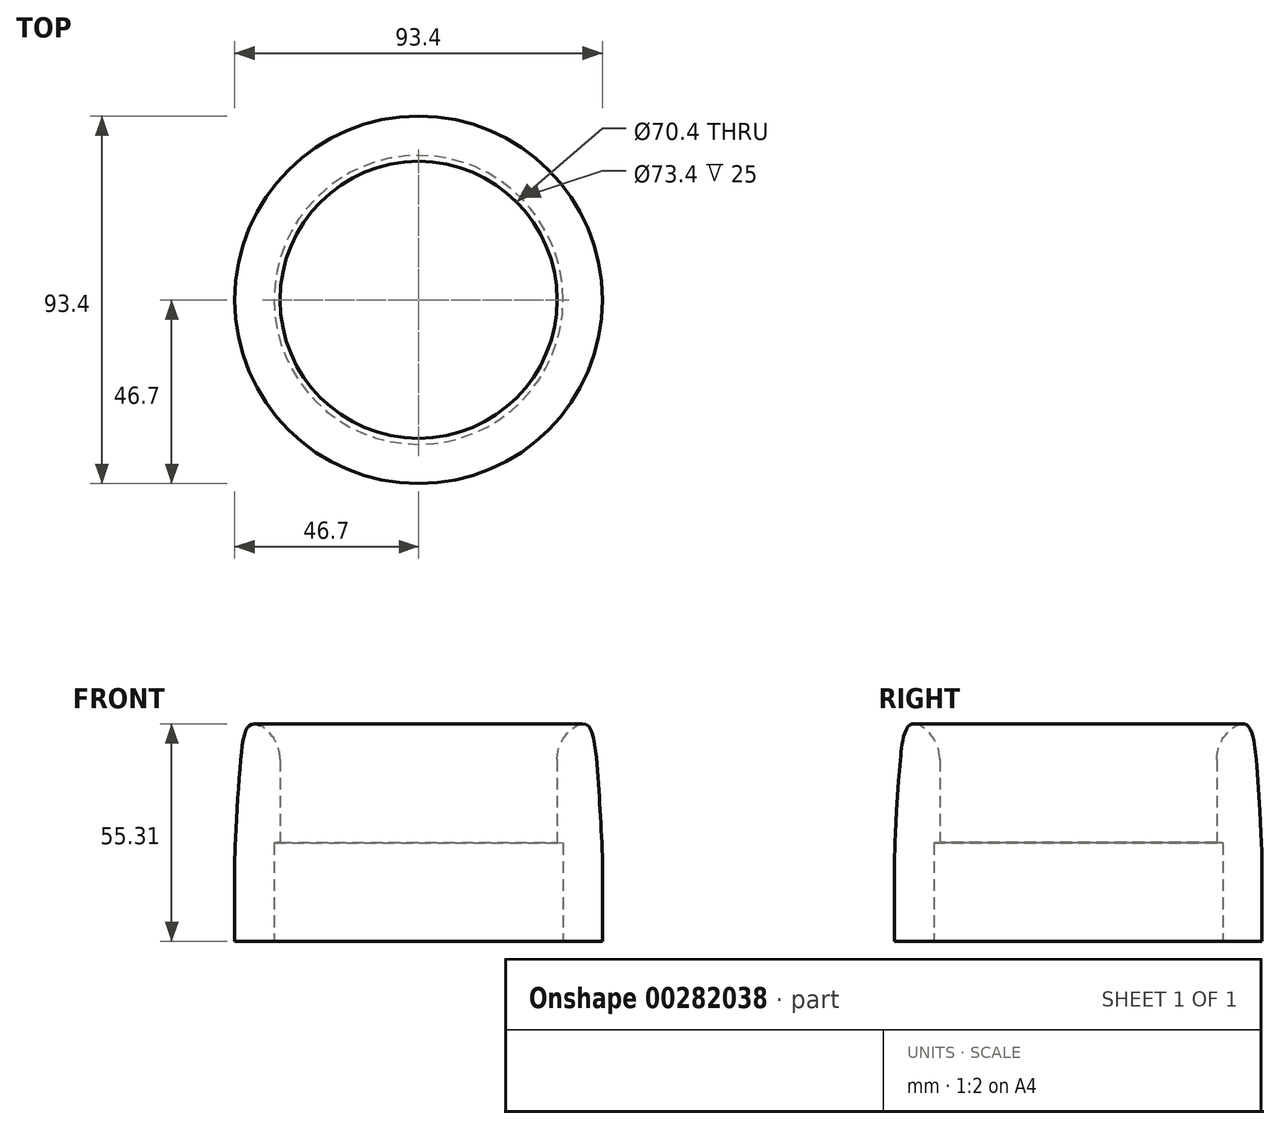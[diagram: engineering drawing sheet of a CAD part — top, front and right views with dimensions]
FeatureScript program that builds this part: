
annotation { "Feature Type Name" : "Feature", "Feature Type Description" : "" }
export const myFeature = defineFeature(function(context is Context, id is Id, definition is map)
    precondition{}
    {
        {
            var Q0;
            Q0=qCreatedBy(makeId("Front.planeOp"),FACE);
            var sketch = newSketch(context, id + "F0", { "sketchPlane" : qUnion([Q0])});
            skLineSegment(sketch, "E0", {"start": v(35.2, 0) * mm, "end": v(35.2, 21) * mm});
            skLineSegment(sketch, "E1", {"start": v(36.7, -25.2) * mm, "end": v(46.7, -25.2) * mm});
            skLineSegment(sketch, "E2", {"start": v(46.7, -25.2) * mm, "end": v(46.7, -5.2) * mm});
            skArc(sketch, "E3", {"start": v(40.2, 29.66) * mm, "mid": v(36.54, 26) * mm, "end": v(35.2, 21) * mm});
            skFitSpline(sketch, "E4", {"points": [v(40.2, 29.66) * mm, v(42.96, 29.66) * mm, v(45.2, 21) * mm, v(46.7, -5.2) * mm], "startDerivative": vector(18.6, 10.94) * mm, "endDerivative": vector(0, -18.9) * mm});
            skLineSegment(sketch, "E5", {"start": v(0, 0) * mm, "end": v(0, 45.07) * mm});
            skLineSegment(sketch, "E6", {"start": v(36.7, -25.2) * mm, "end": v(36.7, -0.2) * mm});
            skLineSegment(sketch, "E7", {"start": v(35.2, 0) * mm, "end": v(36.7, -0.2) * mm});
            skSolve(sketch);
        }
        {
            var Q0;
            Q0=makeQuery(id+"F0.imprint","IMPRINT",FACE,{"disambiguationData":[TD([[makeQuery(id+"F0.imprint","IMPRINT",EDGE,{"derivedFrom":sQuery(id+"F0.wireOp",EDGE,"E0")}),-1.0]])]});
            var Q1;
            Q1=sQuery(id+"F0.wireOp",EDGE,"E5");
            revolve(context, id + "F1", {"entities" : qUnion([Q0]), "axis" : qUnion([Q1]), "revolveType" : RevolveType.FULL});
        }
    });
